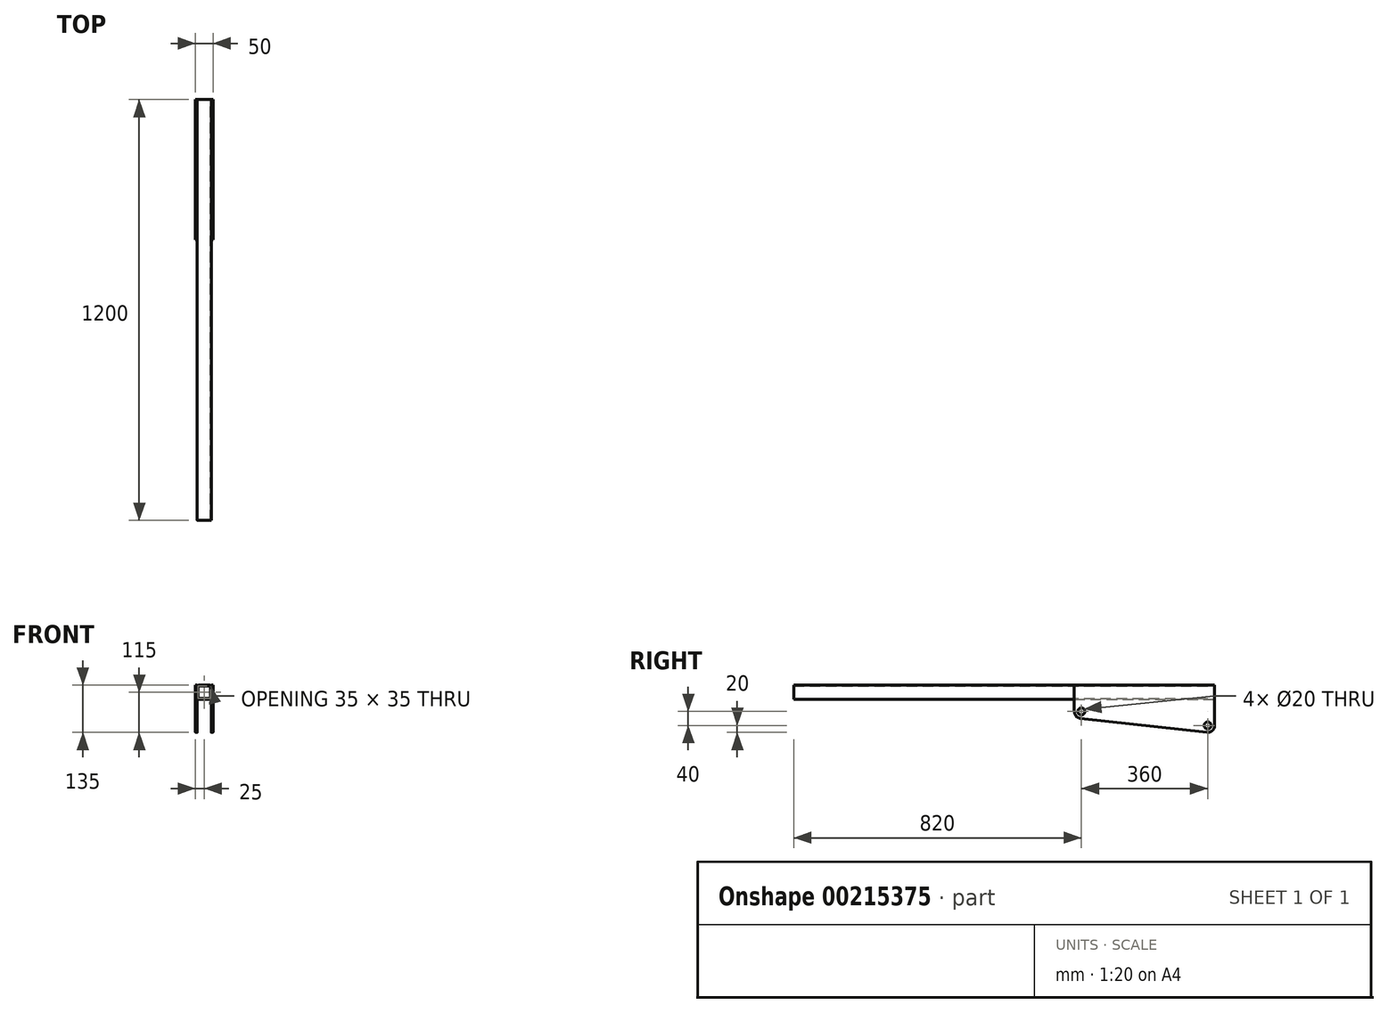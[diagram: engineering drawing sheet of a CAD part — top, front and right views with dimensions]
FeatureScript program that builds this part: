
annotation { "Feature Type Name" : "Feature", "Feature Type Description" : "" }
export const myFeature = defineFeature(function(context is Context, id is Id, definition is map)
    precondition{}
    {
        {
            var Q0;
            Q0=qCreatedBy(makeId("Front.planeOp"),FACE);
            var sketch = newSketch(context, id + "F0", { "sketchPlane" : qUnion([Q0])});
            skLineSegment(sketch, "E0.bottom", {"start": v(15, -20) * mm, "end": v(-15, -20) * mm});
            skLineSegment(sketch, "E0.top", {"start": v(15, 20) * mm, "end": v(-15, 20) * mm});
            skLineSegment(sketch, "E0.left", {"start": v(20, -15) * mm, "end": v(20, 15) * mm});
            skLineSegment(sketch, "E0.right", {"start": v(-20, -15) * mm, "end": v(-20, 15) * mm});
            skPoint(sketch, "E0.middle", {"position": v(0, 0) * mm});
            skPoint(sketch, "E1.visualSharp", {"position": v(-20, 20) * mm});
            skArc(sketch, "E1.filletArc", {"start": v(-15, 20) * mm, "mid": v(-18.54, 18.54) * mm, "end": v(-20, 15) * mm});
            skPoint(sketch, "E2.visualSharp", {"position": v(-20, -20) * mm});
            skArc(sketch, "E2.filletArc", {"start": v(-20, -15) * mm, "mid": v(-18.54, -18.54) * mm, "end": v(-15, -20) * mm});
            skPoint(sketch, "E3.visualSharp", {"position": v(20, -20) * mm});
            skArc(sketch, "E3.filletArc", {"start": v(15, -20) * mm, "mid": v(18.54, -18.54) * mm, "end": v(20, -15) * mm});
            skPoint(sketch, "E4.visualSharp", {"position": v(20, 20) * mm});
            skArc(sketch, "E4.filletArc", {"start": v(20, 15) * mm, "mid": v(18.54, 18.54) * mm, "end": v(15, 20) * mm});
            skSolve(sketch);
        }
        {
            var Q0;
            Q0=qSketchRegion(id+"F0",true);
            var Q1;
            Q1=sQuery(id+"F0.wireOp",EDGE,"E0.top");
            var Q2;
            Q2=sQuery(id+"F0.wireOp",EDGE,"E4.filletArc");
            var Q3;
            Q3=sQuery(id+"F0.wireOp",EDGE,"E0.left");
            var Q4;
            Q4=sQuery(id+"F0.wireOp",EDGE,"E3.filletArc");
            var Q5;
            Q5=sQuery(id+"F0.wireOp",EDGE,"E0.bottom");
            var Q6;
            Q6=sQuery(id+"F0.wireOp",EDGE,"E2.filletArc");
            var Q7;
            Q7=sQuery(id+"F0.wireOp",EDGE,"E0.right");
            var Q8;
            Q8=sQuery(id+"F0.wireOp",EDGE,"E1.filletArc");
            extrude(context, id + "F1", {"entities" : qUnion([Q0]), "surfaceEntities" : qUnion([Q1, Q2, Q3, Q4, Q5, Q6, Q7, Q8]), "endBound" : BoundingType.SYMMETRIC, "depth" : 1200 * mm});
        }
        {
            var Q0;
            Q0=makeQuery(id+"F1.opExtrude","CAP_FACE",FACE,{"disambiguationData":[OSD([sQuery(id+"F0.wireOp",EDGE,"E0.bottom"),sQuery(id+"F0.wireOp",EDGE,"E0.top"),sQuery(id+"F0.wireOp",EDGE,"E0.left"),sQuery(id+"F0.wireOp",EDGE,"E0.right"),sQuery(id+"F0.wireOp",EDGE,"E1.filletArc"),sQuery(id+"F0.wireOp",EDGE,"E2.filletArc"),sQuery(id+"F0.wireOp",EDGE,"E3.filletArc"),sQuery(id+"F0.wireOp",EDGE,"E4.filletArc")])],"isStart":false});
            var Q1;
            Q1=makeQuery(id+"F1.opExtrude","CAP_FACE",FACE,{"disambiguationData":[OSD([sQuery(id+"F0.wireOp",EDGE,"E0.bottom"),sQuery(id+"F0.wireOp",EDGE,"E0.top"),sQuery(id+"F0.wireOp",EDGE,"E0.left"),sQuery(id+"F0.wireOp",EDGE,"E0.right"),sQuery(id+"F0.wireOp",EDGE,"E1.filletArc"),sQuery(id+"F0.wireOp",EDGE,"E2.filletArc"),sQuery(id+"F0.wireOp",EDGE,"E3.filletArc"),sQuery(id+"F0.wireOp",EDGE,"E4.filletArc")])],"isStart":true});
            shell(context, id + "F2", {"entities" : qUnion([Q0, Q1]), "thickness" : 2.5 * mm});
        }
        {
            var Q0;
            Q0=makeQuery(id+"F1.opExtrude","SWEPT_FACE",FACE,{"disambiguationData":[OSD([sQuery(id+"F0.wireOp",EDGE,"E0.left")])]});
            var sketch = newSketch(context, id + "F3", { "sketchPlane" : qUnion([Q0])});
            skLineSegment(sketch, "E5", {"start": v(600, 20) * mm, "end": v(600, -95) * mm});
            skLineSegment(sketch, "E6", {"start": v(200, 20) * mm, "end": v(600, 20) * mm});
            skLineSegment(sketch, "E7", {"start": v(200, 20) * mm, "end": v(200, -55) * mm});
            skLineSegment(sketch, "E8", {"start": v(217.8, -74.88) * mm, "end": v(577.8, -114.88) * mm});
            skPoint(sketch, "E9.visualSharp", {"position": v(200, -72.9) * mm});
            skArc(sketch, "E9.filletArc", {"start": v(200, -55) * mm, "mid": v(205.1, -68.34) * mm, "end": v(217.8, -74.88) * mm});
            skPoint(sketch, "E10.visualSharp", {"position": v(600, -117.35) * mm});
            skArc(sketch, "E10.filletArc", {"start": v(577.8, -114.88) * mm, "mid": v(593.34, -109.9) * mm, "end": v(600, -95) * mm});
            skCircle(sketch, "E11", {"center": v(220, -55) * mm, "radius": 10 * mm});
            skCircle(sketch, "E12", {"center": v(580, -95) * mm, "radius": 10 * mm});
            skSolve(sketch);
        }
        {
            var Q0;
            Q0=makeQuery(id+"F3.imprint","IMPRINT",FACE,{"disambiguationData":[TD([[makeQuery(id+"F3.imprint","IMPRINT",EDGE,{"derivedFrom":sQuery(id+"F3.wireOp",EDGE,"E8")}),1.0]])]});
            var Q1;
            {var subQ0=sQuery(id+"F3.wireOp",EDGE,"E5");var subQ1=sQuery(id+"F0.wireOp",EDGE,"E0.left");var subQ2=makeQuery(id+"F1.opExtrude","SWEPT_EDGE",EDGE,{"disambiguationData":[OSD([subQ1,sQuery(id+"F0.wireOp",EDGE,"E3.filletArc")])]});var subQ3=makeQuery(id+"F3.imprint","INTERSECT",VERTEX,{"derivedFrom":[subQ2,subQ0]});var subQ4=makeQuery(id+"F1.opExtrude","SWEPT_EDGE",EDGE,{"disambiguationData":[OSD([subQ1,sQuery(id+"F0.wireOp",EDGE,"E4.filletArc")])]});var subQ5=makeQuery(id+"F3.imprint","INTERSECT",VERTEX,{"derivedFrom":[subQ4,subQ0]});Q1=makeQuery(id+"F3.imprint","IMPRINT",FACE,{"disambiguationData":[TD([[makeQuery(id+"F3.imprint","IMPRINT",EDGE,{"disambiguationData":[TD([[subQ3,-1.0],[subQ5,1.0]])],"derivedFrom":subQ0}),1.0]])]});}
            var Q2;
            {var subQ3=sQuery(id+"F3.wireOp",EDGE,"E6");Q2=makeQuery(id+"F3.imprint","IMPRINT",FACE,{"disambiguationData":[TD([[makeQuery(id+"F3.imprint","IMPRINT",EDGE,{"derivedFrom":subQ3}),-1.0]])]});}
            extrude(context, id + "F4", {"entities" : qUnion([Q0, Q1, Q2]), "depth" : 5 * mm});
        }
        {
            var Q0;
            Q0=makeQuery(id+"F4.opExtrude","SWEPT_BODY",BODY,{"disambiguationData":[OSD([sQuery(id+"F3.wireOp",EDGE,"E5"),sQuery(id+"F3.wireOp",EDGE,"E6"),sQuery(id+"F3.wireOp",EDGE,"E7"),sQuery(id+"F3.wireOp",EDGE,"E8"),sQuery(id+"F3.wireOp",EDGE,"E9.filletArc"),sQuery(id+"F3.wireOp",EDGE,"E10.filletArc"),sQuery(id+"F3.wireOp",EDGE,"E11"),sQuery(id+"F3.wireOp",EDGE,"E12")])]});
            var Q1;
            Q1=qCreatedBy(makeId("Right.planeOp"),FACE);
            mirror(context, id + "F5", {"entities" : qUnion([Q0]), "mirrorPlane" : qUnion([Q1])});
        }
    });
